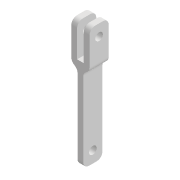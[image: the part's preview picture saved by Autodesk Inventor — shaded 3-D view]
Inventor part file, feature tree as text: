
AUTODESK INVENTOR PART (.ipt)
format: ipt  version: 2022 (Build 260153000, 153)  size: 150,016 bytes
history: native  units: mm
features: extrude x3, sketch x3, projected_geometry x2, other x1, fillet x1
ambient origin geometry x8: Origin, YZ Plane, XZ Plane, XY Plane, X Axis, Y Axis, Z Axis, Center Point
bodies: Body1 (feature_tree)
feature tree (10):
  other  "Sólido1"
  extrude  "Extrusión1"  Depth=3.0mm
  extrude  "Extrusión2"  Depth=9.5mm
  fillet  "Empalme1"  Radius=4.75mm
  extrude  "Extrusión3"  Depth=10.0mm TaperAngle=0.0deg
  sketch  "Boceto1"  dims[d1=3.0mm d2=3.0mm d4=3.0mm]
  sketch  "Boceto2"  dims[d5=3.5mm d6=9.5mm d8=4.75mm]
  projected_geometry  "Contorno proyectado1"
  sketch  "Boceto4"  dims[d9=20.0mm d10=10.0mm d11=0.0mm d13=0.0mm d14=0.0mm d15=4.0mm d16=6.0mm d17=3.0mm d20=3.0mm d25=10.0mm d26=0.0mm d27=65.0mm d28=4.0mm d29=6.0mm]
  projected_geometry  "Contorno proyectado2"
